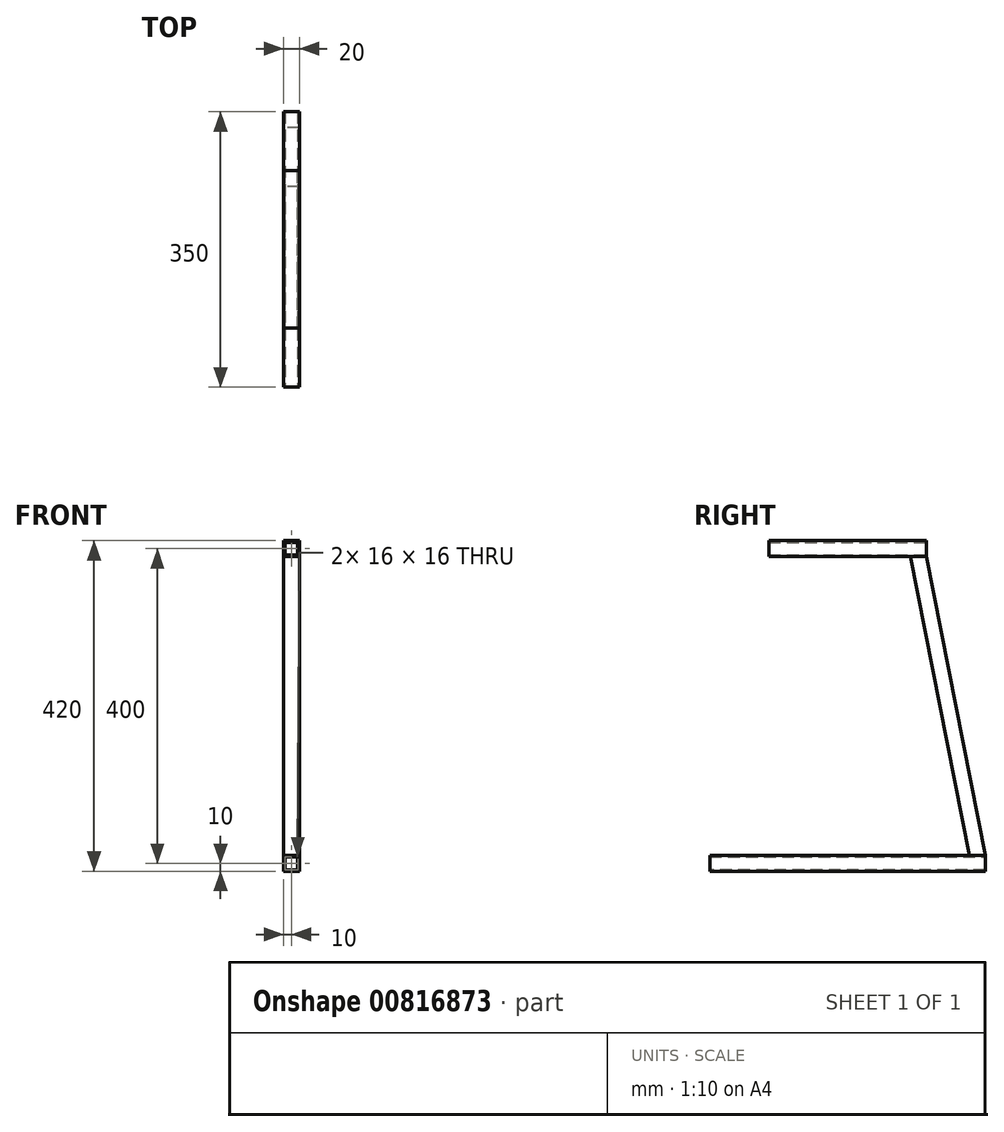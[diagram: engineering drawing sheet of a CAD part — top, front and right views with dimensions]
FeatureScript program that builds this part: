
annotation { "Feature Type Name" : "Feature", "Feature Type Description" : "" }
export const myFeature = defineFeature(function(context is Context, id is Id, definition is map)
    precondition{}
    {
        {
            var Q0;
            Q0=qCreatedBy(makeId("Right.planeOp"),FACE);
            var sketch = newSketch(context, id + "F0", { "sketchPlane" : qUnion([Q0])});
            skLineSegment(sketch, "E0", {"start": v(0, 0) * mm, "end": v(-175, 0) * mm});
            skLineSegment(sketch, "E1", {"start": v(0, 0) * mm, "end": v(175, 0) * mm});
            skLineSegment(sketch, "E2", {"start": v(0, 0) * mm, "end": v(0, 420) * mm, "construction": true});
            skLineSegment(sketch, "E3", {"start": v(0, 420) * mm, "end": v(-100, 420) * mm});
            skLineSegment(sketch, "E4", {"start": v(0, 420) * mm, "end": v(100, 420) * mm});
            skLineSegment(sketch, "E5", {"start": v(-100, 420) * mm, "end": v(-100, 400) * mm});
            skLineSegment(sketch, "E6", {"start": v(-100, 400) * mm, "end": v(100, 400) * mm});
            skLineSegment(sketch, "E7", {"start": v(100, 400) * mm, "end": v(100, 420) * mm});
            skLineSegment(sketch, "E8", {"start": v(-175, 0) * mm, "end": v(-175, 20) * mm});
            skLineSegment(sketch, "E9", {"start": v(-175, 20) * mm, "end": v(175, 20) * mm});
            skLineSegment(sketch, "E10", {"start": v(175, 20) * mm, "end": v(175, 0) * mm});
            skSolve(sketch);
        }
        {
            var Q0;
            Q0 = qSketchRegion(id + "F0", true);
            extrude(context, id + "F1", {"entities" : qUnion([Q0]), "endBound" : BoundingType.SYMMETRIC, "depth" : 20 * mm, "offsetDistance" : 25 * mm});
        }
        {
            var Q0;
            Q0=makeQuery(id+"F1.opExtrude","SWEPT_FACE",FACE,{"disambiguationData":[OSD([sQuery(id+"F0.wireOp",EDGE,"E7")])]});
            var Q1;
            Q1=makeQuery(id+"F1.opExtrude","SWEPT_FACE",FACE,{"disambiguationData":[OSD([sQuery(id+"F0.wireOp",EDGE,"E5")])]});
            var Q2;
            Q2=makeQuery(id+"F1.opExtrude","SWEPT_FACE",FACE,{"disambiguationData":[OSD([sQuery(id+"F0.wireOp",EDGE,"E8")])]});
            var Q3;
            Q3=makeQuery(id+"F1.opExtrude","SWEPT_FACE",FACE,{"disambiguationData":[OSD([sQuery(id+"F0.wireOp",EDGE,"E10")])]});
            shell(context, id + "F2", {"entities" : qUnion([Q0, Q1, Q2, Q3]), "thickness" : 2 * mm});
        }
        {
            var Q0;
            Q0=qCreatedBy(makeId("Right.planeOp"),FACE);
            var sketch = newSketch(context, id + "F3", { "sketchPlane" : qUnion([Q0])});
            skLineSegment(sketch, "E11", {"start": v(100, 400) * mm, "end": v(175, 20) * mm});
            skLineSegment(sketch, "E12.0", {"start": v(79.61, 400) * mm, "end": v(154.61, 20) * mm});
            skLineSegment(sketch, "E13", {"start": v(100, 400) * mm, "end": v(79.61, 400) * mm});
            skLineSegment(sketch, "E14", {"start": v(175, 20) * mm, "end": v(154.61, 20) * mm});
            skSolve(sketch);
        }
        {
            var Q0;
            Q0 = qSketchRegion(id + "F3", true);
            extrude(context, id + "F4", {"entities" : qUnion([Q0]), "endBound" : BoundingType.SYMMETRIC, "depth" : 20 * mm, "offsetDistance" : 25 * mm});
        }
    });
